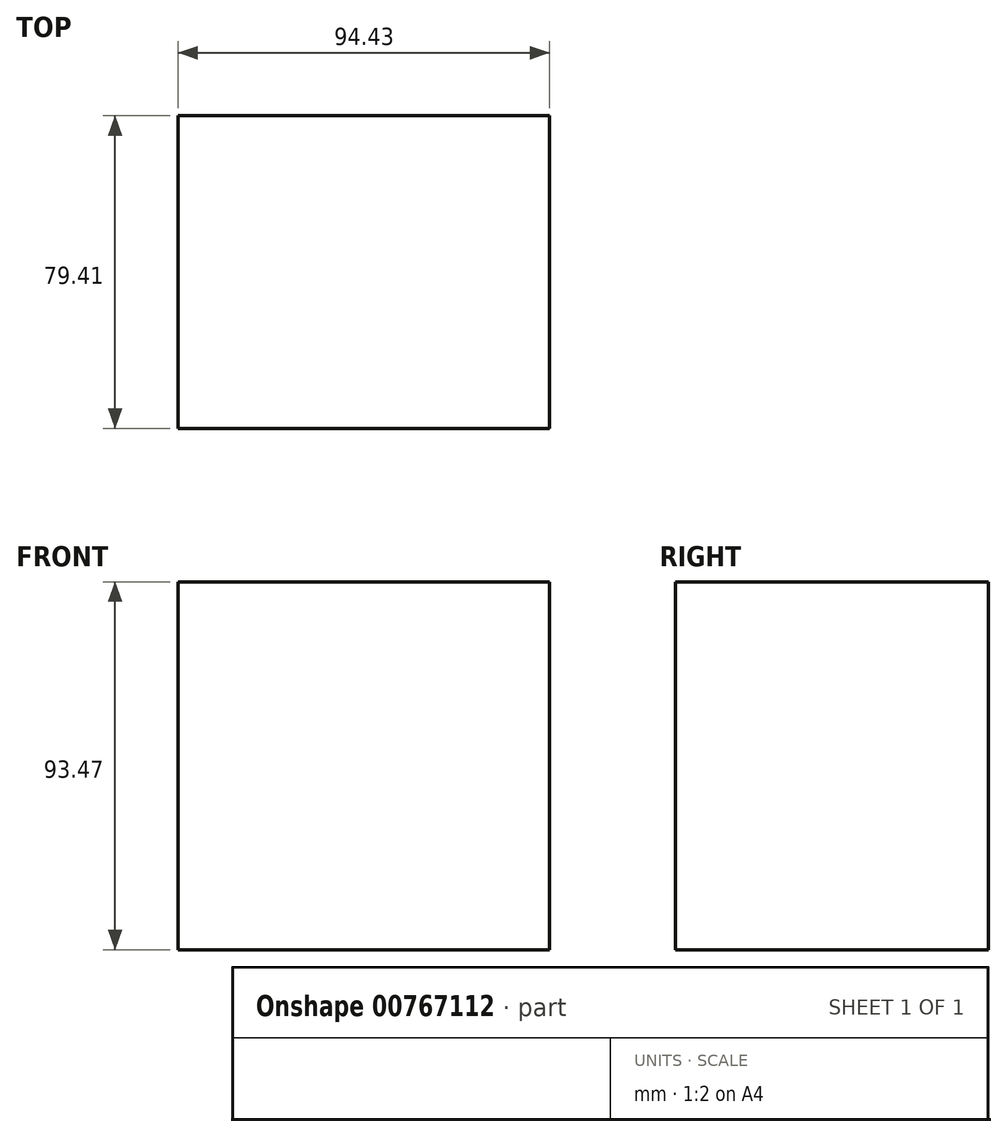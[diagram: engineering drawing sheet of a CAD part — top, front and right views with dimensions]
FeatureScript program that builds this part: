
annotation { "Feature Type Name" : "Feature", "Feature Type Description" : "" }
export const myFeature = defineFeature(function(context is Context, id is Id, definition is map)
    precondition{}
    {
        {
            var Q0;
            Q0=qCreatedBy(makeId("Top.planeOp"),FACE);
            var sketch = newSketch(context, id + "F0", { "sketchPlane" : qUnion([Q0])});
            skLineSegment(sketch, "E0.bottom", {"start": v(-46.62, 33.37) * mm, "end": v(47.8, 33.37) * mm});
            skLineSegment(sketch, "E0.top", {"start": v(-46.62, -46.04) * mm, "end": v(47.8, -46.04) * mm});
            skLineSegment(sketch, "E0.left", {"start": v(-46.62, 33.37) * mm, "end": v(-46.62, -46.04) * mm});
            skLineSegment(sketch, "E0.right", {"start": v(47.8, 33.37) * mm, "end": v(47.8, -46.04) * mm});
            skSolve(sketch);
        }
        {
            var Q0;
            Q0=makeQuery(id+"F0.imprint","IMPRINT",FACE,{"disambiguationData":[TD([[makeQuery(id+"F0.imprint","IMPRINT",EDGE,{"derivedFrom":sQuery(id+"F0.wireOp",EDGE,"E0.bottom")}),-1.0]])]});
            extrude(context, id + "F1", {"entities" : qUnion([Q0]), "depth" : 93.47 * mm, "offsetDistance" : 25.4 * mm});
        }
    });
